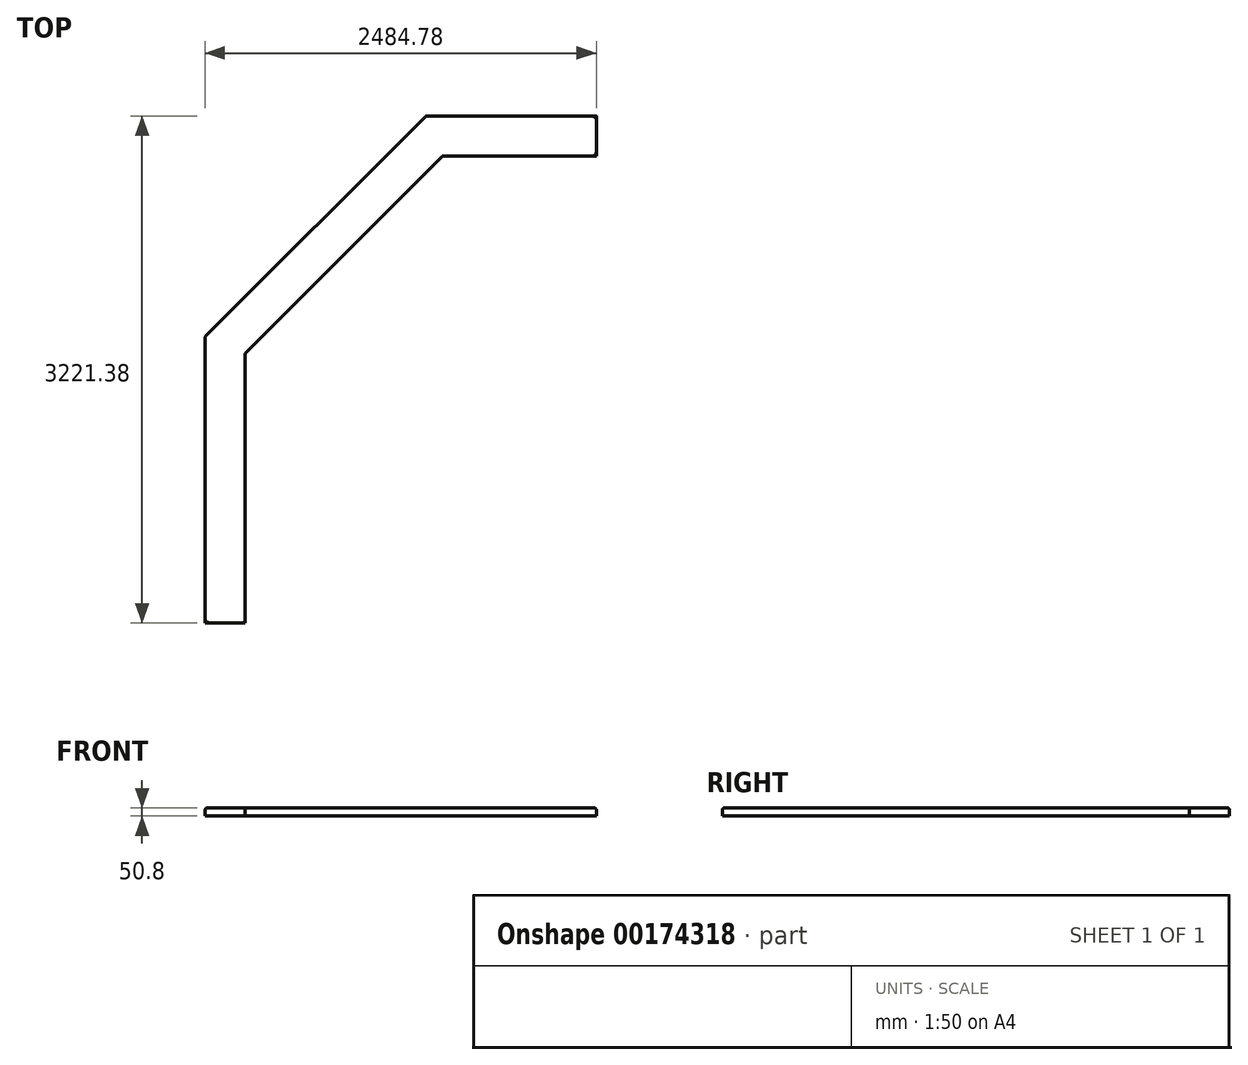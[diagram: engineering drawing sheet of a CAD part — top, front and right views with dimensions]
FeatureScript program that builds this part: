
annotation { "Feature Type Name" : "Feature", "Feature Type Description" : "" }
export const myFeature = defineFeature(function(context is Context, id is Id, definition is map)
    precondition{}
    {
        {
            var Q0;
            Q0=qCreatedBy(makeId("Top.planeOp"),FACE);
            var sketch = newSketch(context, id + "F0", { "sketchPlane" : qUnion([Q0])});
            skLineSegment(sketch, "E0.bottom", {"start": v(52.6, -127) * mm, "end": v(1028.7, -127) * mm});
            skLineSegment(sketch, "E0.top", {"start": v(0, 127) * mm, "end": v(1028.7, 127) * mm});
            skLineSegment(sketch, "E0.right", {"start": v(1028.7, -127) * mm, "end": v(1028.7, 127) * mm});
            skLineSegment(sketch, "E1", {"start": v(-1456.08, -1276.47) * mm, "end": v(-52.6, 127) * mm});
            skLineSegment(sketch, "E2", {"start": v(0, 127) * mm, "end": v(-52.6, 127) * mm});
            skPoint(sketch, "E3.orphan", {"position": v(0, -127) * mm});
            skLineSegment(sketch, "E4.top", {"start": v(-1456.08, -3094.38) * mm, "end": v(-1202.08, -3094.38) * mm});
            skLineSegment(sketch, "E4.left", {"start": v(-1456.08, -1329.08) * mm, "end": v(-1456.08, -3094.38) * mm});
            skLineSegment(sketch, "E4.right", {"start": v(-1202.08, -1381.68) * mm, "end": v(-1202.08, -3094.38) * mm});
            skLineSegment(sketch, "E5", {"start": v(-1456.08, -1329.08) * mm, "end": v(-1456.08, -1276.47) * mm});
            skLineSegment(sketch, "E6.trimOffspring", {"start": v(-1202.08, -1381.68) * mm, "end": v(52.6, -127) * mm});
            skPoint(sketch, "E4.bottom.end.orphan", {"position": v(-1329.08, -1329.08) * mm});
            skSolve(sketch);
        }
        {
            var Q0;
            Q0 = qSketchRegion(id + "F0", true);
            extrude(context, id + "F1", {"entities" : qUnion([Q0]), "depth" : 50.8 * mm});
        }
        {
            var Q0;
            Q0=makeQuery(id+"F1.opExtrude","CAP_FACE",FACE,{"disambiguationData":[OSD([sQuery(id+"F0.wireOp",EDGE,"E0.bottom"),sQuery(id+"F0.wireOp",EDGE,"E0.top"),sQuery(id+"F0.wireOp",EDGE,"E0.right"),sQuery(id+"F0.wireOp",EDGE,"E1"),sQuery(id+"F0.wireOp",EDGE,"E2"),sQuery(id+"F0.wireOp",EDGE,"E4.top"),sQuery(id+"F0.wireOp",EDGE,"E4.left"),sQuery(id+"F0.wireOp",EDGE,"E4.right"),sQuery(id+"F0.wireOp",EDGE,"E5"),sQuery(id+"F0.wireOp",EDGE,"E6.trimOffspring")])],"isStart":false});
            var Q1;
            Q1=makeQuery(id+"F1.opExtrude","SWEPT_EDGE",EDGE,{"disambiguationData":[OSD([sQuery(id+"F0.wireOp",EDGE,"E1"),sQuery(id+"F0.wireOp",EDGE,"E5")])]});
            var Q2;
            Q2=makeQuery(id+"F1.opExtrude","SWEPT_EDGE",EDGE,{"disambiguationData":[OSD([sQuery(id+"F0.wireOp",EDGE,"E1"),sQuery(id+"F0.wireOp",EDGE,"E2")])]});
            var Q3;
            Q3=makeQuery(id+"F1.opExtrude","SWEPT_EDGE",EDGE,{"disambiguationData":[OSD([sQuery(id+"F0.wireOp",EDGE,"E0.bottom"),sQuery(id+"F0.wireOp",EDGE,"E6.trimOffspring")])]});
            var Q4;
            Q4=makeQuery(id+"F1.opExtrude","SWEPT_EDGE",EDGE,{"disambiguationData":[OSD([sQuery(id+"F0.wireOp",EDGE,"E4.right"),sQuery(id+"F0.wireOp",EDGE,"E6.trimOffspring")])]});
            fillet(context, id + "F2", {"entities" : qUnion([Q0, Q1, Q2, Q3, Q4]), "radius" : 12.7 * mm, "tangentPropagation" : true, "allowEdgeOverflow" : false});
        }
        {
            var Q0;
            Q0=makeQuery(id+"F1.opExtrude","SWEPT_BODY",BODY,{"disambiguationData":[OSD([sQuery(id+"F0.wireOp",EDGE,"E0.bottom"),sQuery(id+"F0.wireOp",EDGE,"E0.top"),sQuery(id+"F0.wireOp",EDGE,"E0.right"),sQuery(id+"F0.wireOp",EDGE,"E1"),sQuery(id+"F0.wireOp",EDGE,"E2"),sQuery(id+"F0.wireOp",EDGE,"E4.top"),sQuery(id+"F0.wireOp",EDGE,"E4.left"),sQuery(id+"F0.wireOp",EDGE,"E4.right"),sQuery(id+"F0.wireOp",EDGE,"E5"),sQuery(id+"F0.wireOp",EDGE,"E6.trimOffspring")])]});
            transform(context, id + "F3", {"entities" : qUnion([Q0]), "transformType" : TransformType.TRANSLATION_3D, "dx" : -63.5 * mm, "dy" : 0 * mm, "dz" : -203.2 * mm, "makeCopy" : false});
        }
    });
